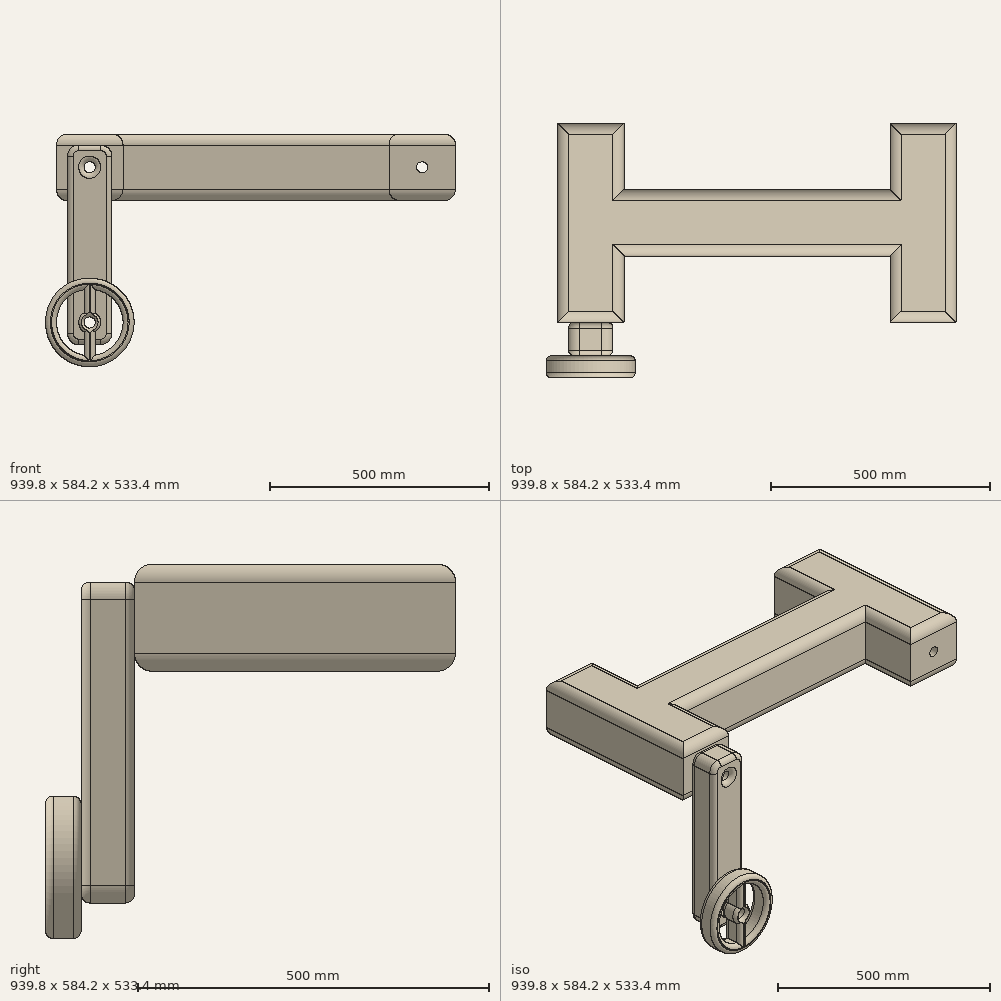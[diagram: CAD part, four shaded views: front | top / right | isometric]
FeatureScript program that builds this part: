
annotation { "Feature Type Name" : "Feature", "Feature Type Description" : "" }
export const myFeature = defineFeature(function(context is Context, id is Id, definition is map)
    precondition{}
    {
        {
            var Q0;
            Q0=qCreatedBy(makeId("Top.planeOp"),FACE);
            var sketch = newSketch(context, id + "F0", { "sketchPlane" : qUnion([Q0])});
            skLineSegment(sketch, "E0.bottom", {"start": v(-457.2, 228.6) * mm, "end": v(457.2, 228.6) * mm, "construction": true});
            skLineSegment(sketch, "E0.top", {"start": v(-457.2, -228.6) * mm, "end": v(-304.8, -228.6) * mm});
            skLineSegment(sketch, "E0.left", {"start": v(-457.2, 228.6) * mm, "end": v(-457.2, -228.6) * mm});
            skLineSegment(sketch, "E0.right", {"start": v(457.2, 228.6) * mm, "end": v(457.2, -228.6) * mm});
            skPoint(sketch, "E1", {"position": v(0, 228.6) * mm});
            skPoint(sketch, "E2", {"position": v(457.2, 0) * mm});
            skLineSegment(sketch, "E3", {"start": v(304.8, 228.6) * mm, "end": v(304.8, -228.6) * mm, "construction": true});
            skLineSegment(sketch, "E4.MirrorCS", {"start": v(-304.8, 228.6) * mm, "end": v(-304.8, -228.6) * mm, "construction": true});
            skLineSegment(sketch, "E5", {"start": v(304.8, 76.2) * mm, "end": v(-304.8, 76.2) * mm});
            skLineSegment(sketch, "E6", {"start": v(457.2, 0) * mm, "end": v(-304.8, 0) * mm, "construction": true});
            skLineSegment(sketch, "E7.MirrorCS", {"start": v(304.8, -76.2) * mm, "end": v(-304.8, -76.2) * mm});
            skLineSegment(sketch, "E8", {"start": v(304.8, 76.2) * mm, "end": v(304.8, 228.6) * mm});
            skLineSegment(sketch, "E9", {"start": v(304.8, -76.2) * mm, "end": v(304.8, -228.6) * mm});
            skLineSegment(sketch, "E10", {"start": v(-304.8, -76.2) * mm, "end": v(-304.8, -228.6) * mm});
            skLineSegment(sketch, "E11", {"start": v(-304.8, 76.2) * mm, "end": v(-304.8, 228.6) * mm});
            skLineSegment(sketch, "E12", {"start": v(304.8, 228.6) * mm, "end": v(457.2, 228.6) * mm});
            skLineSegment(sketch, "E13", {"start": v(-304.8, 228.6) * mm, "end": v(-457.2, 228.6) * mm});
            skLineSegment(sketch, "E14.trimOffspring", {"start": v(304.8, -228.6) * mm, "end": v(457.2, -228.6) * mm});
            skSolve(sketch);
        }
        {
            var Q0;
            Q0 = qSketchRegion(id + "F0", true);
            extrude(context, id + "F1", {"entities" : qUnion([Q0]), "depth" : 152.4 * mm, "offsetDistance" : 25.4 * mm});
        }
        {
            var Q0;
            Q0=makeQuery(id+"F1.opExtrude","SWEPT_FACE",FACE,{"disambiguationData":[OSD([sQuery(id+"F0.wireOp",EDGE,"E12")])]});
            var sketch = newSketch(context, id + "F2", { "sketchPlane" : qUnion([Q0])});
            skLineSegment(sketch, "E15", {"start": v(-457.2, 76.2) * mm, "end": v(479.01, 76.2) * mm, "construction": true});
            skCircle(sketch, "E16", {"center": v(-381, 76.2) * mm, "radius": 12.7 * mm});
            skCircle(sketch, "E17.MirrorC", {"center": v(381, 76.2) * mm, "radius": 12.7 * mm});
            skSolve(sketch);
        }
        {
            var Q0;
            Q0 = qSketchRegion(id + "F2", true);
            var Q1;
            Q1=makeQuery(id+"F1.opExtrude","SWEPT_FACE",FACE,{"disambiguationData":[OSD([sQuery(id+"F0.wireOp",EDGE,"E0.top")])]});
            extrude(context, id + "F3", {"entities" : qUnion([Q0]), "operationType" : NewBodyOperationType.REMOVE, "endBound" : BoundingType.UP_TO_SURFACE, "oppositeDirection" : true, "depth" : 25.4 * mm, "endBoundEntityFace" : qUnion([Q1]), "offsetDistance" : 25.4 * mm});
        }
        {
            var Q0;
            Q0=makeQuery(id+"F1.opExtrude","SWEPT_FACE",FACE,{"disambiguationData":[OSD([sQuery(id+"F0.wireOp",EDGE,"E0.top")])]});
            var sketch = newSketch(context, id + "F4", { "sketchPlane" : qUnion([Q0])});
            skLineSegment(sketch, "E18", {"start": v(-381, 76.2) * mm, "end": v(-489.65, 76.2) * mm, "construction": true});
            skLineSegment(sketch, "E19.bottom", {"start": v(-406.4, 127) * mm, "end": v(-355.6, 127) * mm});
            skLineSegment(sketch, "E19.top", {"start": v(-406.4, -330.2) * mm, "end": v(-355.6, -330.2) * mm});
            skLineSegment(sketch, "E19.left", {"start": v(-431.8, 101.6) * mm, "end": v(-431.8, -304.8) * mm});
            skLineSegment(sketch, "E19.right", {"start": v(-330.2, 101.6) * mm, "end": v(-330.2, -304.8) * mm});
            skLineSegment(sketch, "E20", {"start": v(-381, 76.2) * mm, "end": v(-381, 152.4) * mm, "construction": true});
            skPoint(sketch, "E21", {"position": v(-381, 127) * mm});
            skLineSegment(sketch, "E22", {"start": v(-381, 127) * mm, "end": v(-381, -330.2) * mm, "construction": true});
            skCircle(sketch, "E23", {"center": v(-381, 76.2) * mm, "radius": 12.7 * mm});
            skPoint(sketch, "E24.visualSharp", {"position": v(-431.8, 127) * mm});
            skArc(sketch, "E24.filletArc", {"start": v(-406.4, 127) * mm, "mid": v(-424.36, 119.56) * mm, "end": v(-431.8, 101.6) * mm});
            skPoint(sketch, "E25.visualSharp", {"position": v(-330.2, 127) * mm});
            skArc(sketch, "E25.filletArc", {"start": v(-330.2, 101.6) * mm, "mid": v(-337.64, 119.56) * mm, "end": v(-355.6, 127) * mm});
            skPoint(sketch, "E26.visualSharp", {"position": v(-330.2, -330.2) * mm});
            skArc(sketch, "E26.filletArc", {"start": v(-355.6, -330.2) * mm, "mid": v(-337.64, -322.76) * mm, "end": v(-330.2, -304.8) * mm});
            skPoint(sketch, "E27.visualSharp", {"position": v(-431.8, -330.2) * mm});
            skArc(sketch, "E27.filletArc", {"start": v(-431.8, -304.8) * mm, "mid": v(-424.36, -322.76) * mm, "end": v(-406.4, -330.2) * mm});
            skPoint(sketch, "E28", {"position": v(-431.8, -101.6) * mm});
            skLineSegment(sketch, "E29", {"start": v(-431.8, -101.6) * mm, "end": v(-330.2, -101.6) * mm, "construction": true});
            skCircle(sketch, "E30.MirrorC", {"center": v(-381, -279.4) * mm, "radius": 12.7 * mm});
            skSolve(sketch);
        }
        {
            var Q0;
            Q0 = qSketchRegion(id + "F4", true);
            extrude(context, id + "F5", {"entities" : qUnion([Q0]), "depth" : 76.2 * mm, "offsetDistance" : 25.4 * mm});
        }
        {
            var Q0;
            Q0=makeQuery(id+"F5.opExtrude","CAP_FACE",FACE,{"disambiguationData":[OSD([sQuery(id+"F4.wireOp",EDGE,"E19.bottom"),sQuery(id+"F4.wireOp",EDGE,"E19.top"),sQuery(id+"F4.wireOp",EDGE,"E19.left"),sQuery(id+"F4.wireOp",EDGE,"E19.right"),sQuery(id+"F4.wireOp",EDGE,"E23"),sQuery(id+"F4.wireOp",EDGE,"E24.filletArc"),sQuery(id+"F4.wireOp",EDGE,"E25.filletArc"),sQuery(id+"F4.wireOp",EDGE,"E26.filletArc"),sQuery(id+"F4.wireOp",EDGE,"E27.filletArc"),sQuery(id+"F4.wireOp",EDGE,"E30.MirrorC")])],"isStart":false});
            var sketch = newSketch(context, id + "F6", { "sketchPlane" : qUnion([Q0])});
            skCircle(sketch, "E31", {"center": v(-381, -279.4) * mm, "radius": 101.6 * mm});
            skArc(sketch, "E32", {"start": v(-393.7, -204.27) * mm, "mid": v(-457.2, -279.4) * mm, "end": v(-393.7, -354.53) * mm});
            skLineSegment(sketch, "E33", {"start": v(-393.7, -257.4) * mm, "end": v(-393.7, -204.27) * mm, "construction": true});
            skLineSegment(sketch, "E34", {"start": v(-381, -279.4) * mm, "end": v(-431.8, -279.4) * mm, "construction": true});
            skLineSegment(sketch, "E35", {"start": v(-381, -279.4) * mm, "end": v(-381, -242.18) * mm, "construction": true});
            skLineSegment(sketch, "E36.MirrorCS", {"start": v(-368.3, -257.4) * mm, "end": v(-368.3, -204.27) * mm, "construction": true});
            skLineSegment(sketch, "E37", {"start": v(-393.7, -204.27) * mm, "end": v(-393.7, -257.4) * mm});
            skLineSegment(sketch, "E38.MirrorCS", {"start": v(-368.3, -204.27) * mm, "end": v(-368.3, -257.4) * mm});
            skArc(sketch, "E39.trimOffspring", {"start": v(-368.3, -354.53) * mm, "mid": v(-304.8, -279.4) * mm, "end": v(-368.3, -204.27) * mm});
            skArc(sketch, "E40", {"start": v(-393.7, -257.4) * mm, "mid": v(-406.4, -279.4) * mm, "end": v(-393.7, -301.4) * mm});
            skPoint(sketch, "E41.orphan", {"position": v(-393.7, -279.4) * mm});
            skPoint(sketch, "E42.orphan", {"position": v(-368.3, -279.4) * mm});
            skLineSegment(sketch, "E43.trimOffspring", {"start": v(-368.3, -301.4) * mm, "end": v(-368.3, -354.53) * mm});
            skLineSegment(sketch, "E44.trimOffspring", {"start": v(-393.7, -301.4) * mm, "end": v(-393.7, -354.53) * mm});
            skArc(sketch, "E45.trimOffspring", {"start": v(-368.3, -301.4) * mm, "mid": v(-355.6, -279.4) * mm, "end": v(-368.3, -257.4) * mm});
            skCircle(sketch, "E46", {"center": v(-381, -279.4) * mm, "radius": 12.7 * mm});
            skSolve(sketch);
        }
        {
            var Q0;
            Q0 = qSketchRegion(id + "F6", true);
            extrude(context, id + "F7", {"entities" : qUnion([Q0]), "depth" : 50.8 * mm, "offsetDistance" : 25.4 * mm});
        }
        {
            var Q0;
            Q0=makeQuery(id+"F1.opExtrude","CAP_FACE",FACE,{"disambiguationData":[OSD([sQuery(id+"F0.wireOp",EDGE,"E0.top"),sQuery(id+"F0.wireOp",EDGE,"E0.left"),sQuery(id+"F0.wireOp",EDGE,"E0.right"),sQuery(id+"F0.wireOp",EDGE,"E5"),sQuery(id+"F0.wireOp",EDGE,"E7.MirrorCS"),sQuery(id+"F0.wireOp",EDGE,"E8"),sQuery(id+"F0.wireOp",EDGE,"E9"),sQuery(id+"F0.wireOp",EDGE,"E10"),sQuery(id+"F0.wireOp",EDGE,"E11"),sQuery(id+"F0.wireOp",EDGE,"E12"),sQuery(id+"F0.wireOp",EDGE,"E13"),sQuery(id+"F0.wireOp",EDGE,"E14.trimOffspring")])],"isStart":false});
            var Q1;
            Q1=makeQuery(id+"F1.opExtrude","CAP_FACE",FACE,{"disambiguationData":[OSD([sQuery(id+"F0.wireOp",EDGE,"E0.top"),sQuery(id+"F0.wireOp",EDGE,"E0.left"),sQuery(id+"F0.wireOp",EDGE,"E0.right"),sQuery(id+"F0.wireOp",EDGE,"E5"),sQuery(id+"F0.wireOp",EDGE,"E7.MirrorCS"),sQuery(id+"F0.wireOp",EDGE,"E8"),sQuery(id+"F0.wireOp",EDGE,"E9"),sQuery(id+"F0.wireOp",EDGE,"E10"),sQuery(id+"F0.wireOp",EDGE,"E11"),sQuery(id+"F0.wireOp",EDGE,"E12"),sQuery(id+"F0.wireOp",EDGE,"E13"),sQuery(id+"F0.wireOp",EDGE,"E14.trimOffspring")])],"isStart":true});
            fillet(context, id + "F8", {"entities" : qUnion([Q0, Q1]), "radius" : 25.4 * mm, "tangentPropagation" : true, "allowEdgeOverflow" : false});
        }
        {
            var Q0;
            Q0=makeQuery(id+"F5.opExtrude","CAP_FACE",FACE,{"disambiguationData":[OSD([sQuery(id+"F4.wireOp",EDGE,"E19.bottom"),sQuery(id+"F4.wireOp",EDGE,"E19.top"),sQuery(id+"F4.wireOp",EDGE,"E19.left"),sQuery(id+"F4.wireOp",EDGE,"E19.right"),sQuery(id+"F4.wireOp",EDGE,"E23"),sQuery(id+"F4.wireOp",EDGE,"E24.filletArc"),sQuery(id+"F4.wireOp",EDGE,"E25.filletArc"),sQuery(id+"F4.wireOp",EDGE,"E26.filletArc"),sQuery(id+"F4.wireOp",EDGE,"E27.filletArc"),sQuery(id+"F4.wireOp",EDGE,"E30.MirrorC")])],"isStart":false});
            var Q1;
            Q1=makeQuery(id+"F5.opExtrude","CAP_FACE",FACE,{"disambiguationData":[OSD([sQuery(id+"F4.wireOp",EDGE,"E19.bottom"),sQuery(id+"F4.wireOp",EDGE,"E19.top"),sQuery(id+"F4.wireOp",EDGE,"E19.left"),sQuery(id+"F4.wireOp",EDGE,"E19.right"),sQuery(id+"F4.wireOp",EDGE,"E23"),sQuery(id+"F4.wireOp",EDGE,"E24.filletArc"),sQuery(id+"F4.wireOp",EDGE,"E25.filletArc"),sQuery(id+"F4.wireOp",EDGE,"E26.filletArc"),sQuery(id+"F4.wireOp",EDGE,"E27.filletArc"),sQuery(id+"F4.wireOp",EDGE,"E30.MirrorC")])],"isStart":true});
            fillet(context, id + "F9", {"entities" : qUnion([Q0, Q1]), "radius" : 12.7 * mm, "tangentPropagation" : true, "allowEdgeOverflow" : false});
        }
        {
            var Q0;
            Q0=makeQuery(id+"F7.opExtrude","CAP_FACE",FACE,{"disambiguationData":[OSD([sQuery(id+"F6.wireOp",EDGE,"E31"),sQuery(id+"F6.wireOp",EDGE,"E32"),sQuery(id+"F6.wireOp",EDGE,"E37"),sQuery(id+"F6.wireOp",EDGE,"E38.MirrorCS"),sQuery(id+"F6.wireOp",EDGE,"E39.trimOffspring"),sQuery(id+"F6.wireOp",EDGE,"E40"),sQuery(id+"F6.wireOp",EDGE,"E43.trimOffspring"),sQuery(id+"F6.wireOp",EDGE,"E44.trimOffspring"),sQuery(id+"F6.wireOp",EDGE,"E45.trimOffspring"),sQuery(id+"F6.wireOp",EDGE,"E46")])],"isStart":false});
            var Q1;
            Q1=makeQuery(id+"F7.opExtrude","CAP_FACE",FACE,{"disambiguationData":[OSD([sQuery(id+"F6.wireOp",EDGE,"E31"),sQuery(id+"F6.wireOp",EDGE,"E32"),sQuery(id+"F6.wireOp",EDGE,"E37"),sQuery(id+"F6.wireOp",EDGE,"E38.MirrorCS"),sQuery(id+"F6.wireOp",EDGE,"E39.trimOffspring"),sQuery(id+"F6.wireOp",EDGE,"E40"),sQuery(id+"F6.wireOp",EDGE,"E43.trimOffspring"),sQuery(id+"F6.wireOp",EDGE,"E44.trimOffspring"),sQuery(id+"F6.wireOp",EDGE,"E45.trimOffspring"),sQuery(id+"F6.wireOp",EDGE,"E46")])],"isStart":true});
            fillet(context, id + "F10", {"entities" : qUnion([Q0, Q1]), "radius" : 11.43 * mm, "tangentPropagation" : true, "allowEdgeOverflow" : false});
        }
    });
